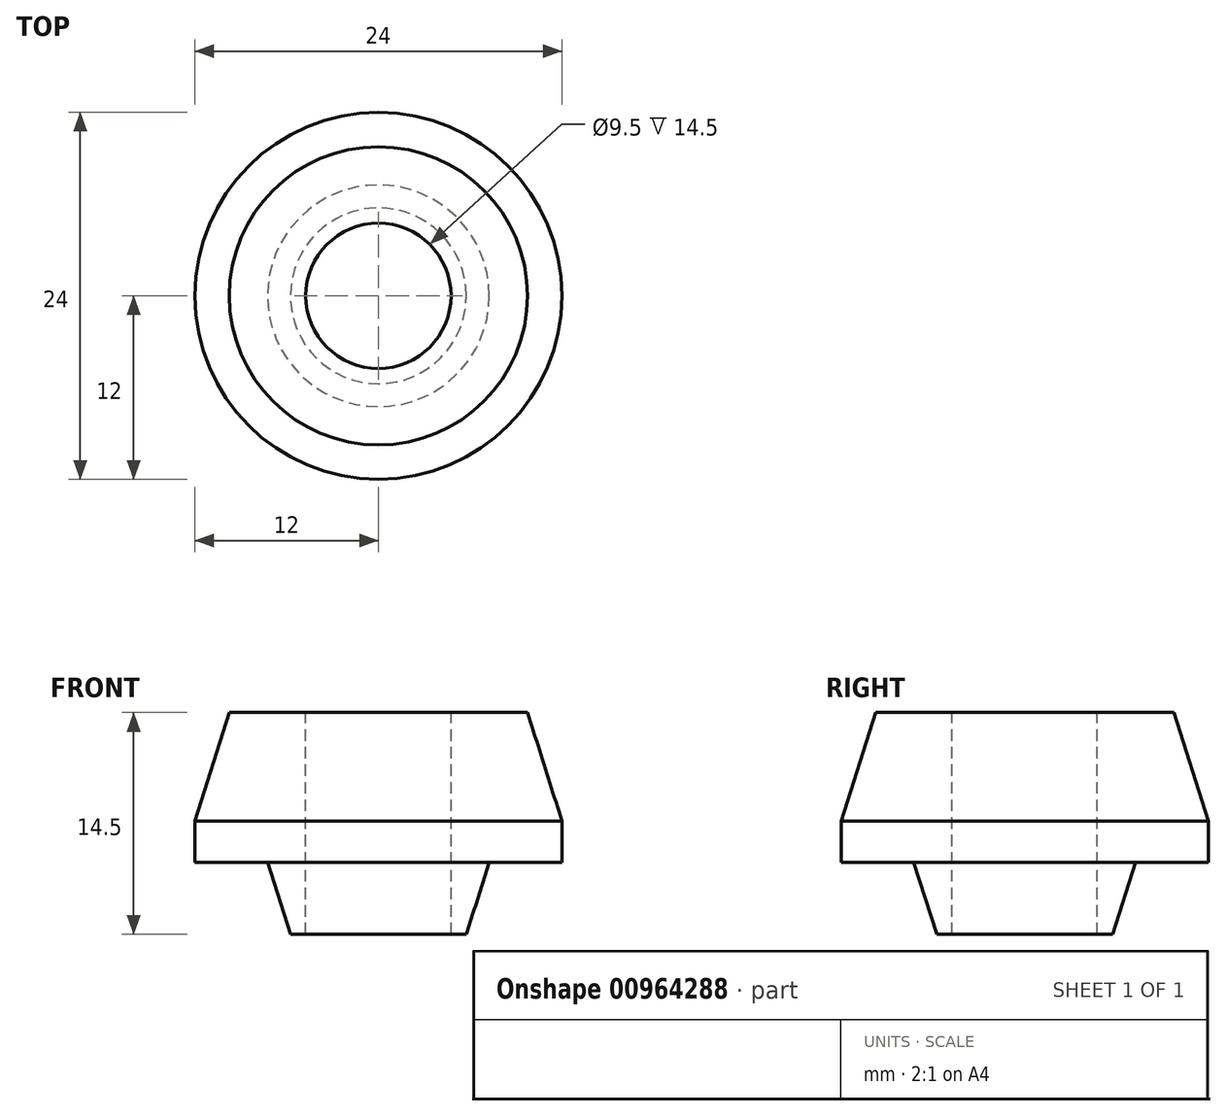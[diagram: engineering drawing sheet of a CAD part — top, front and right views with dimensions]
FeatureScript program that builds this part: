
annotation { "Feature Type Name" : "Feature", "Feature Type Description" : "" }
export const myFeature = defineFeature(function(context is Context, id is Id, definition is map)
    precondition{}
    {
        {
            var Q0;
            Q0=qCreatedBy(makeId("Front.planeOp"),FACE);
            var sketch = newSketch(context, id + "F0", { "sketchPlane" : qUnion([Q0])});
            skLineSegment(sketch, "E0", {"start": v(0, 0) * mm, "end": v(0, -10.02) * mm, "construction": true});
            skLineSegment(sketch, "E1", {"start": v(4.75, 0) * mm, "end": v(4.75, -14.5) * mm});
            skLineSegment(sketch, "E2", {"start": v(4.75, 0) * mm, "end": v(9.75, 0) * mm});
            skLineSegment(sketch, "E3", {"start": v(9.75, 0) * mm, "end": v(12, -7.1) * mm});
            skLineSegment(sketch, "E4", {"start": v(12, -7.1) * mm, "end": v(12, -9.8) * mm});
            skLineSegment(sketch, "E5", {"start": v(12, -9.8) * mm, "end": v(7.25, -9.8) * mm});
            skLineSegment(sketch, "E6", {"start": v(7.25, -9.8) * mm, "end": v(5.75, -14.5) * mm});
            skLineSegment(sketch, "E7", {"start": v(4.75, -14.5) * mm, "end": v(5.75, -14.5) * mm});
            skSolve(sketch);
        }
        {
            var Q0;
            Q0 = qSketchRegion(id + "F0", true);
            var Q1;
            Q1=sQuery(id+"F0.wireOp",EDGE,"E0");
            revolve(context, id + "F1", {"surfaceOperationType" : NewSurfaceOperationType.NEW, "entities" : qUnion([Q0]), "axis" : qUnion([Q1]), "revolveType" : RevolveType.FULL});
        }
    });
